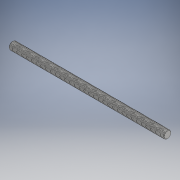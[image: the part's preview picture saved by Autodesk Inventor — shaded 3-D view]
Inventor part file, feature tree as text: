
AUTODESK INVENTOR PART (.ipt)
format: ipt  version: 2019 (Build 230136000, 136)  size: 2,290,176 bytes
history: native  units: mm
features: mirror x1
ambient origin geometry x8: Origin, YZ Plane, XZ Plane, XY Plane, X Axis, Y Axis, Z Axis, Center Point
bodies: Solid1 (feature_tree)
feature tree (1):
  mirror  "Mirror1"
